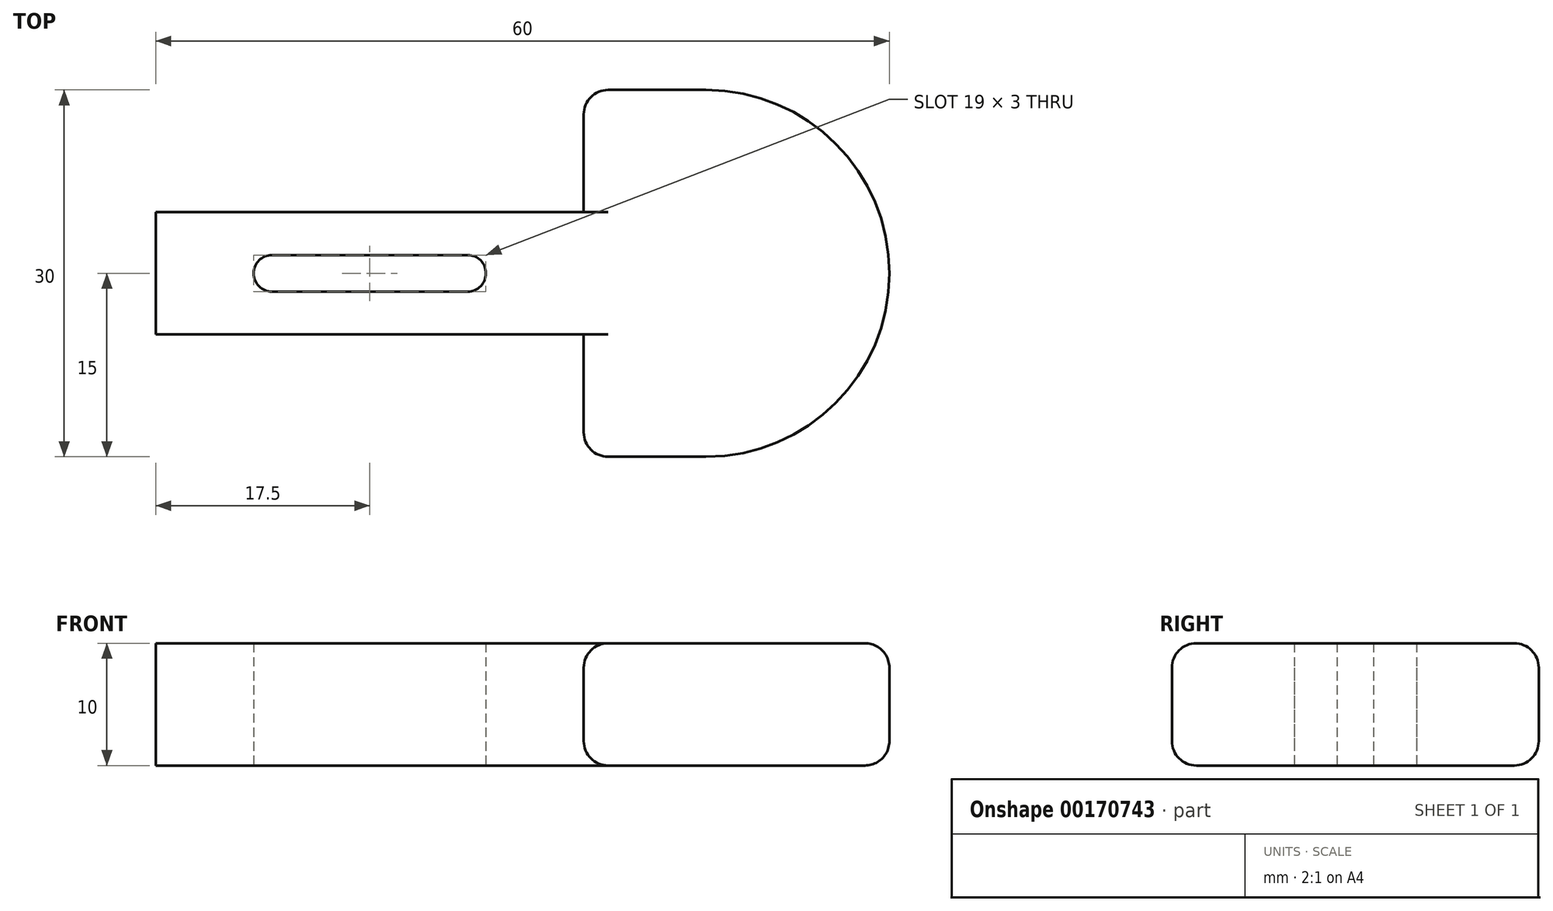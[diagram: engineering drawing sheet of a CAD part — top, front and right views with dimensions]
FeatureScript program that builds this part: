
annotation { "Feature Type Name" : "Feature", "Feature Type Description" : "" }
export const myFeature = defineFeature(function(context is Context, id is Id, definition is map)
    precondition{}
    {
        {
            var Q0;
            Q0=qCreatedBy(makeId("Top.planeOp"),FACE);
            var sketch = newSketch(context, id + "F0", { "sketchPlane" : qUnion([Q0])});
            skLineSegment(sketch, "E0.bottom", {"start": v(17.5, 5) * mm, "end": v(-17.5, 5) * mm});
            skLineSegment(sketch, "E0.top", {"start": v(17.5, -5) * mm, "end": v(-17.5, -5) * mm});
            skLineSegment(sketch, "E0.right", {"start": v(-17.5, 5) * mm, "end": v(-17.5, -5) * mm});
            skPoint(sketch, "E0.middle", {"position": v(0, 0) * mm});
            skLineSegment(sketch, "E1", {"start": v(0, 0) * mm, "end": v(8, 0) * mm});
            skLineSegment(sketch, "E2", {"start": v(0, 0) * mm, "end": v(-8, 0) * mm});
            skArc(sketch, "E3.0.startCap", {"start": v(0, 1.5) * mm, "mid": v(1.5, 0) * mm, "end": v(0, -1.5) * mm});
            skArc(sketch, "E3.0.endCap", {"start": v(-8, -1.5) * mm, "mid": v(-9.5, 0) * mm, "end": v(-8, 1.5) * mm});
            skLineSegment(sketch, "E3.0.left", {"start": v(0, -1.5) * mm, "end": v(-8, -1.5) * mm});
            skLineSegment(sketch, "E3.0.right", {"start": v(0, 1.5) * mm, "end": v(-8, 1.5) * mm});
            skArc(sketch, "E3.1.startCap", {"start": v(0, -1.5) * mm, "mid": v(-1.5, 0) * mm, "end": v(0, 1.5) * mm});
            skArc(sketch, "E3.1.endCap", {"start": v(8, 1.5) * mm, "mid": v(9.5, 0) * mm, "end": v(8, -1.5) * mm});
            skLineSegment(sketch, "E3.1.left", {"start": v(0, 1.5) * mm, "end": v(8, 1.5) * mm});
            skLineSegment(sketch, "E3.1.right", {"start": v(0, -1.5) * mm, "end": v(8, -1.5) * mm});
            skLineSegment(sketch, "E4.bottom", {"start": v(17.5, 15) * mm, "end": v(27.5, 15) * mm});
            skLineSegment(sketch, "E4.top", {"start": v(17.5, -15) * mm, "end": v(27.5, -15) * mm});
            skLineSegment(sketch, "E4.left", {"start": v(17.5, 15) * mm, "end": v(17.5, -15) * mm});
            skLineSegment(sketch, "E4.right", {"start": v(27.5, 15) * mm, "end": v(27.5, -15) * mm});
            skArc(sketch, "E5", {"start": v(27.5, -15) * mm, "mid": v(42.5, 0) * mm, "end": v(27.5, 15) * mm});
            skSolve(sketch);
        }
        {
            var Q0;
            Q0=makeQuery(id+"F0.imprint","IMPRINT",FACE,{"disambiguationData":[TD([[makeQuery(id+"F0.imprint","IMPRINT",EDGE,{"derivedFrom":sQuery(id+"F0.wireOp",EDGE,"E0.left")}),1.0]])]});
            var Q1;
            Q1=makeQuery(id+"F0.imprint","IMPRINT",FACE,{"disambiguationData":[TD([[makeQuery(id+"F0.imprint","IMPRINT",EDGE,{"derivedFrom":sQuery(id+"F0.wireOp",EDGE,"E0.bottom")}),1.0]])]});
            var Q2;
            {var subQ3=sQuery(id+"F0.wireOp",EDGE,"E4.bottom");Q2=makeQuery(id+"F0.imprint","IMPRINT",FACE,{"disambiguationData":[TD([[makeQuery(id+"F0.imprint","IMPRINT",EDGE,{"derivedFrom":subQ3}),-1.0]])]});}
            var Q3;
            Q3=makeQuery(id+"F0.imprint","IMPRINT",FACE,{"disambiguationData":[TD([[makeQuery(id+"F0.imprint","IMPRINT",EDGE,{"derivedFrom":sQuery(id+"F0.wireOp",EDGE,"E4.right")}),1.0]])]});
            extrude(context, id + "F1", {"entities" : qUnion([Q0, Q1, Q2, Q3]), "depth" : 10 * mm});
        }
        {
            var Q0;
            Q0=makeQuery(id+"F1.opExtrude","SWEPT_EDGE",EDGE,{"disambiguationData":[OSD([sQuery(id+"F0.wireOp",EDGE,"E4.bottom"),sQuery(id+"F0.wireOp",EDGE,"E4.right"),sQuery(id+"F0.wireOp",EDGE,"E5")])]});
            var Q1;
            Q1=makeQuery(id+"F1.opExtrude","SWEPT_EDGE",EDGE,{"disambiguationData":[OSD([sQuery(id+"F0.wireOp",EDGE,"E4.top"),sQuery(id+"F0.wireOp",EDGE,"E4.right"),sQuery(id+"F0.wireOp",EDGE,"E5")])]});
            var Q2;
            Q2=makeQuery(id+"F1.opExtrude","CAP_EDGE",EDGE,{"disambiguationData":[OSD([sQuery(id+"F0.wireOp",EDGE,"E5")])],"isStart":false});
            var Q3;
            Q3=makeQuery(id+"F1.opExtrude","CAP_EDGE",EDGE,{"disambiguationData":[OSD([sQuery(id+"F0.wireOp",EDGE,"E5")])],"isStart":true});
            var Q4;
            {var subQ0=sQuery(id+"F0.wireOp",EDGE,"E4.left");Q4=makeQuery(id+"F1.opExtrude","CAP_EDGE",EDGE,{"disambiguationData":[OSD([subQ0]),TDD([makeQuery(id+"F0.imprint","IMPRINT",EDGE,{"disambiguationData":[TD([[makeQuery(id+"F0.imprint","INTERSECT",VERTEX,{"derivedFrom":[sQuery(id+"F0.wireOp",EDGE,"E0.bottom"),subQ0]}),1.0]])],"derivedFrom":subQ0})])],"isStart":false});}
            var Q5;
            {var subQ0=sQuery(id+"F0.wireOp",EDGE,"E4.left");Q5=makeQuery(id+"F1.opExtrude","CAP_EDGE",EDGE,{"disambiguationData":[OSD([subQ0]),TDD([makeQuery(id+"F0.imprint","IMPRINT",EDGE,{"disambiguationData":[TD([[makeQuery(id+"F0.imprint","INTERSECT",VERTEX,{"derivedFrom":[sQuery(id+"F0.wireOp",EDGE,"E0.top"),subQ0]}),-1.0]])],"derivedFrom":subQ0})])],"isStart":false});}
            var Q6;
            Q6=makeQuery(id+"F1.opExtrude","SWEPT_EDGE",EDGE,{"disambiguationData":[OSD([sQuery(id+"F0.wireOp",EDGE,"E4.top"),sQuery(id+"F0.wireOp",EDGE,"E4.left")])]});
            var Q7;
            {var subQ0=sQuery(id+"F0.wireOp",EDGE,"E4.left");Q7=makeQuery(id+"F1.opExtrude","CAP_EDGE",EDGE,{"disambiguationData":[OSD([subQ0]),TDD([makeQuery(id+"F0.imprint","IMPRINT",EDGE,{"disambiguationData":[TD([[makeQuery(id+"F0.imprint","INTERSECT",VERTEX,{"derivedFrom":[sQuery(id+"F0.wireOp",EDGE,"E0.bottom"),subQ0]}),1.0]])],"derivedFrom":subQ0})])],"isStart":true});}
            var Q8;
            {var subQ0=sQuery(id+"F0.wireOp",EDGE,"E4.left");Q8=makeQuery(id+"F1.opExtrude","CAP_EDGE",EDGE,{"disambiguationData":[OSD([subQ0]),TDD([makeQuery(id+"F0.imprint","IMPRINT",EDGE,{"disambiguationData":[TD([[makeQuery(id+"F0.imprint","INTERSECT",VERTEX,{"derivedFrom":[sQuery(id+"F0.wireOp",EDGE,"E0.top"),subQ0]}),-1.0]])],"derivedFrom":subQ0})])],"isStart":true});}
            var Q9;
            Q9=makeQuery(id+"F1.opExtrude","SWEPT_EDGE",EDGE,{"disambiguationData":[OSD([sQuery(id+"F0.wireOp",EDGE,"E4.bottom"),sQuery(id+"F0.wireOp",EDGE,"E4.left")])]});
            fillet(context, id + "F2", {"entities" : qUnion([Q0, Q1, Q2, Q3, Q4, Q5, Q6, Q7, Q8, Q9]), "radius" : 2 * mm, "tangentPropagation" : true, "allowEdgeOverflow" : false});
        }
    });
